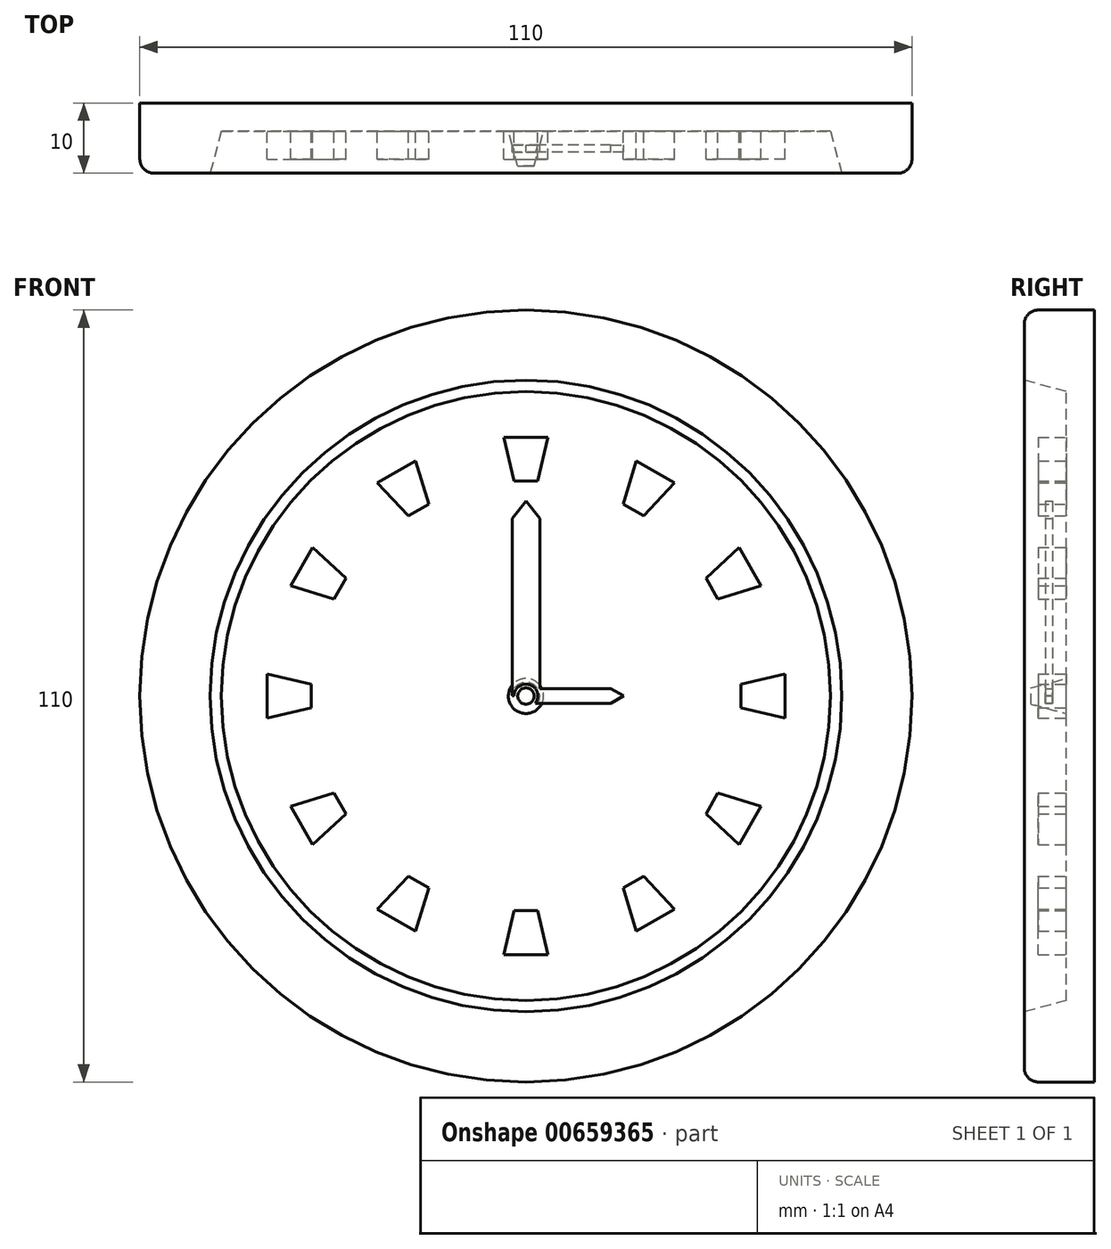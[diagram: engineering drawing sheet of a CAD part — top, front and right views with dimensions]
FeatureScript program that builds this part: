
annotation { "Feature Type Name" : "Feature", "Feature Type Description" : "" }
export const myFeature = defineFeature(function(context is Context, id is Id, definition is map)
    precondition{}
    {
        {
            var Q0;
            Q0=qCreatedBy(makeId("Front.planeOp"),FACE);
            var sketch = newSketch(context, id + "F0", { "sketchPlane" : qUnion([Q0])});
            skCircle(sketch, "E0", {"center": v(0, 0) * mm, "radius": 55 * mm});
            skSolve(sketch);
        }
        {
            var Q0;
            Q0 = qSketchRegion(id + "F0", true);
            extrude(context, id + "F1", {"entities" : qUnion([Q0]), "depth" : 10 * mm, "offsetDistance" : 25 * mm});
        }
        {
            var Q0;
            Q0=makeQuery(id+"F1.opExtrude","CAP_FACE",FACE,{"disambiguationData":[OSD([sQuery(id+"F0.wireOp",EDGE,"E0")])],"isStart":false});
            var sketch = newSketch(context, id + "F2", { "sketchPlane" : qUnion([Q0])});
            skCircle(sketch, "E1", {"center": v(0, 0) * mm, "radius": 45 * mm});
            skSolve(sketch);
        }
        {
            var Q0;
            Q0 = qSketchRegion(id + "F2", true);
            extrude(context, id + "F3", {"entities" : qUnion([Q0]), "operationType" : NewBodyOperationType.REMOVE, "oppositeDirection" : true, "depth" : 6 * mm, "offsetDistance" : 25 * mm, "hasDraft" : true, "draftAngle" : 15 * degree, "draftPullDirection" : true});
        }
        {
            var Q0;
            Q0=makeQuery(id+"F3.boolean.opBoolean","COPY",FACE,{"derivedFrom":makeQuery(id+"F3.opExtrude","CAP_FACE",FACE,{"disambiguationData":[OSD([sQuery(id+"F2.wireOp",EDGE,"E1")])],"isStart":false})});
            var sketch = newSketch(context, id + "F4", { "sketchPlane" : qUnion([Q0])});
            skLineSegment(sketch, "E2", {"start": v(-3.13, 36.9) * mm, "end": v(0, 36.9) * mm});
            skLineSegment(sketch, "E3", {"start": v(0, 36.9) * mm, "end": v(3.13, 36.9) * mm});
            skLineSegment(sketch, "E4", {"start": v(-1.7, 30.6) * mm, "end": v(0, 30.6) * mm});
            skLineSegment(sketch, "E5", {"start": v(0, 30.6) * mm, "end": v(1.7, 30.6) * mm});
            skLineSegment(sketch, "E6", {"start": v(-3.13, 36.9) * mm, "end": v(-1.7, 30.6) * mm});
            skLineSegment(sketch, "E7", {"start": v(3.13, 36.9) * mm, "end": v(1.7, 30.6) * mm});
            skLineSegment(sketch, "E8.1.0", {"start": v(15.73, 33.52) * mm, "end": v(18.45, 31.95) * mm});
            skLineSegment(sketch, "E8.1.1", {"start": v(18.45, 31.95) * mm, "end": v(21.16, 30.38) * mm});
            skLineSegment(sketch, "E8.1.2", {"start": v(15.73, 33.52) * mm, "end": v(13.84, 27.35) * mm});
            skLineSegment(sketch, "E8.1.3", {"start": v(13.84, 27.35) * mm, "end": v(15.3, 26.5) * mm});
            skLineSegment(sketch, "E8.1.4", {"start": v(15.3, 26.5) * mm, "end": v(16.77, 25.66) * mm});
            skLineSegment(sketch, "E8.1.5", {"start": v(21.16, 30.38) * mm, "end": v(16.77, 25.66) * mm});
            skLineSegment(sketch, "E8.2.0", {"start": v(30.38, 21.16) * mm, "end": v(31.95, 18.45) * mm});
            skLineSegment(sketch, "E8.2.1", {"start": v(31.95, 18.45) * mm, "end": v(33.52, 15.73) * mm});
            skLineSegment(sketch, "E8.2.2", {"start": v(30.38, 21.16) * mm, "end": v(25.66, 16.77) * mm});
            skLineSegment(sketch, "E8.2.3", {"start": v(25.66, 16.77) * mm, "end": v(26.5, 15.3) * mm});
            skLineSegment(sketch, "E8.2.4", {"start": v(26.5, 15.3) * mm, "end": v(27.35, 13.84) * mm});
            skLineSegment(sketch, "E8.2.5", {"start": v(33.52, 15.73) * mm, "end": v(27.35, 13.84) * mm});
            skLineSegment(sketch, "E8.3.0", {"start": v(36.9, 3.13) * mm, "end": v(36.9, 0) * mm});
            skLineSegment(sketch, "E8.3.1", {"start": v(36.9, 0) * mm, "end": v(36.9, -3.13) * mm});
            skLineSegment(sketch, "E8.3.2", {"start": v(36.9, 3.13) * mm, "end": v(30.6, 1.7) * mm});
            skLineSegment(sketch, "E8.3.3", {"start": v(30.6, 1.7) * mm, "end": v(30.6, 0) * mm});
            skLineSegment(sketch, "E8.3.4", {"start": v(30.6, 0) * mm, "end": v(30.6, -1.7) * mm});
            skLineSegment(sketch, "E8.3.5", {"start": v(36.9, -3.13) * mm, "end": v(30.6, -1.7) * mm});
            skLineSegment(sketch, "E8.4.0", {"start": v(33.52, -15.73) * mm, "end": v(31.95, -18.45) * mm});
            skLineSegment(sketch, "E8.4.1", {"start": v(31.95, -18.45) * mm, "end": v(30.38, -21.16) * mm});
            skLineSegment(sketch, "E8.4.2", {"start": v(33.52, -15.73) * mm, "end": v(27.35, -13.84) * mm});
            skLineSegment(sketch, "E8.4.3", {"start": v(27.35, -13.84) * mm, "end": v(26.5, -15.3) * mm});
            skLineSegment(sketch, "E8.4.4", {"start": v(26.5, -15.3) * mm, "end": v(25.66, -16.77) * mm});
            skLineSegment(sketch, "E8.4.5", {"start": v(30.38, -21.16) * mm, "end": v(25.66, -16.77) * mm});
            skLineSegment(sketch, "E8.5.0", {"start": v(21.16, -30.38) * mm, "end": v(18.45, -31.95) * mm});
            skLineSegment(sketch, "E8.5.1", {"start": v(18.45, -31.95) * mm, "end": v(15.73, -33.52) * mm});
            skLineSegment(sketch, "E8.5.2", {"start": v(21.16, -30.38) * mm, "end": v(16.77, -25.66) * mm});
            skLineSegment(sketch, "E8.5.3", {"start": v(16.77, -25.66) * mm, "end": v(15.3, -26.5) * mm});
            skLineSegment(sketch, "E8.5.4", {"start": v(15.3, -26.5) * mm, "end": v(13.84, -27.35) * mm});
            skLineSegment(sketch, "E8.5.5", {"start": v(15.73, -33.52) * mm, "end": v(13.84, -27.35) * mm});
            skLineSegment(sketch, "E8.6.0", {"start": v(3.13, -36.9) * mm, "end": v(0, -36.9) * mm});
            skLineSegment(sketch, "E8.6.1", {"start": v(0, -36.9) * mm, "end": v(-3.13, -36.9) * mm});
            skLineSegment(sketch, "E8.6.2", {"start": v(3.13, -36.9) * mm, "end": v(1.7, -30.6) * mm});
            skLineSegment(sketch, "E8.6.3", {"start": v(1.7, -30.6) * mm, "end": v(0, -30.6) * mm});
            skLineSegment(sketch, "E8.6.4", {"start": v(0, -30.6) * mm, "end": v(-1.7, -30.6) * mm});
            skLineSegment(sketch, "E8.6.5", {"start": v(-3.13, -36.9) * mm, "end": v(-1.7, -30.6) * mm});
            skLineSegment(sketch, "E8.7.0", {"start": v(-15.73, -33.52) * mm, "end": v(-18.45, -31.95) * mm});
            skLineSegment(sketch, "E8.7.1", {"start": v(-18.45, -31.95) * mm, "end": v(-21.16, -30.38) * mm});
            skLineSegment(sketch, "E8.7.2", {"start": v(-15.73, -33.52) * mm, "end": v(-13.84, -27.35) * mm});
            skLineSegment(sketch, "E8.7.3", {"start": v(-13.84, -27.35) * mm, "end": v(-15.3, -26.5) * mm});
            skLineSegment(sketch, "E8.7.4", {"start": v(-15.3, -26.5) * mm, "end": v(-16.77, -25.66) * mm});
            skLineSegment(sketch, "E8.7.5", {"start": v(-21.16, -30.38) * mm, "end": v(-16.77, -25.66) * mm});
            skLineSegment(sketch, "E8.8.0", {"start": v(-30.38, -21.16) * mm, "end": v(-31.95, -18.45) * mm});
            skLineSegment(sketch, "E8.8.1", {"start": v(-31.95, -18.45) * mm, "end": v(-33.52, -15.73) * mm});
            skLineSegment(sketch, "E8.8.2", {"start": v(-30.38, -21.16) * mm, "end": v(-25.66, -16.77) * mm});
            skLineSegment(sketch, "E8.8.3", {"start": v(-25.66, -16.77) * mm, "end": v(-26.5, -15.3) * mm});
            skLineSegment(sketch, "E8.8.4", {"start": v(-26.5, -15.3) * mm, "end": v(-27.35, -13.84) * mm});
            skLineSegment(sketch, "E8.8.5", {"start": v(-33.52, -15.73) * mm, "end": v(-27.35, -13.84) * mm});
            skLineSegment(sketch, "E8.9.0", {"start": v(-36.9, -3.13) * mm, "end": v(-36.9, 0) * mm});
            skLineSegment(sketch, "E8.9.1", {"start": v(-36.9, 0) * mm, "end": v(-36.9, 3.13) * mm});
            skLineSegment(sketch, "E8.9.2", {"start": v(-36.9, -3.13) * mm, "end": v(-30.6, -1.7) * mm});
            skLineSegment(sketch, "E8.9.3", {"start": v(-30.6, -1.7) * mm, "end": v(-30.6, 0) * mm});
            skLineSegment(sketch, "E8.9.4", {"start": v(-30.6, 0) * mm, "end": v(-30.6, 1.7) * mm});
            skLineSegment(sketch, "E8.9.5", {"start": v(-36.9, 3.13) * mm, "end": v(-30.6, 1.7) * mm});
            skLineSegment(sketch, "E8.10.0", {"start": v(-33.52, 15.73) * mm, "end": v(-31.95, 18.45) * mm});
            skLineSegment(sketch, "E8.10.1", {"start": v(-31.95, 18.45) * mm, "end": v(-30.38, 21.16) * mm});
            skLineSegment(sketch, "E8.10.2", {"start": v(-33.52, 15.73) * mm, "end": v(-27.35, 13.84) * mm});
            skLineSegment(sketch, "E8.10.3", {"start": v(-27.35, 13.84) * mm, "end": v(-26.5, 15.3) * mm});
            skLineSegment(sketch, "E8.10.4", {"start": v(-26.5, 15.3) * mm, "end": v(-25.66, 16.77) * mm});
            skLineSegment(sketch, "E8.10.5", {"start": v(-30.38, 21.16) * mm, "end": v(-25.66, 16.77) * mm});
            skLineSegment(sketch, "E8.11.0", {"start": v(-21.16, 30.38) * mm, "end": v(-18.45, 31.95) * mm});
            skLineSegment(sketch, "E8.11.1", {"start": v(-18.45, 31.95) * mm, "end": v(-15.73, 33.52) * mm});
            skLineSegment(sketch, "E8.11.2", {"start": v(-21.16, 30.38) * mm, "end": v(-16.77, 25.66) * mm});
            skLineSegment(sketch, "E8.11.3", {"start": v(-16.77, 25.66) * mm, "end": v(-15.3, 26.5) * mm});
            skLineSegment(sketch, "E8.11.4", {"start": v(-15.3, 26.5) * mm, "end": v(-13.84, 27.35) * mm});
            skLineSegment(sketch, "E8.11.5", {"start": v(-15.73, 33.52) * mm, "end": v(-13.84, 27.35) * mm});
            skPoint(sketch, "E8.center", {"position": v(0, 0) * mm});
            skLineSegment(sketch, "E8.anchor1", {"start": v(0, 0) * mm, "end": v(-3.13, 36.9) * mm, "construction": true});
            skLineSegment(sketch, "E8.anchor2", {"start": v(0, 0) * mm, "end": v(-21.16, 30.38) * mm, "construction": true});
            skSolve(sketch);
        }
        {
            var Q0;
            Q0 = qSketchRegion(id + "F4", true);
            extrude(context, id + "F5", {"entities" : qUnion([Q0]), "operationType" : NewBodyOperationType.ADD, "depth" : 4 * mm, "offsetDistance" : 25 * mm});
        }
        {
            var Q0;
            Q0=makeQuery(id+"F1.opExtrude","CAP_FACE",FACE,{"disambiguationData":[OSD([sQuery(id+"F0.wireOp",EDGE,"E0")])],"isStart":false});
            cPlane(context, id + "F6", {"entities" : qUnion([Q0]), "cplaneType" : CPlaneType.OFFSET, "offset" : 0 * mm, "width" : 150 * mm, "height" : 150 * mm});
        }
        {
            var Q0;
            Q0=qCreatedBy(id+"F6.planeOp",FACE);
            var sketch = newSketch(context, id + "F7", { "sketchPlane" : qUnion([Q0])});
            skText(sketch, "E9", { "text": "10", "fontName": "OpenSans-Regular.ttf"});
            skText(sketch, "E10", { "text": "12", "fontName": "OpenSans-Regular.ttf"});
            skText(sketch, "E11", { "text": "9\n", "fontName": "OpenSans-Regular.ttf"});
            skText(sketch, "E12", { "text": "8\n", "fontName": "OpenSans-Regular.ttf"});
            skText(sketch, "E13", { "text": "7\n", "fontName": "OpenSans-Regular.ttf"});
            skText(sketch, "E14", { "text": "6\n", "fontName": "OpenSans-Regular.ttf"});
            skText(sketch, "E15", { "text": "5\n", "fontName": "OpenSans-Regular.ttf"});
            skText(sketch, "E16", { "text": "4\n", "fontName": "OpenSans-Regular.ttf"});
            skText(sketch, "E17", { "text": "3\n", "fontName": "OpenSans-Regular.ttf"});
            skText(sketch, "E18", { "text": "2", "fontName": "OpenSans-Regular.ttf"});
            skText(sketch, "E19", { "text": "1", "fontName": "OpenSans-Regular.ttf"});
            skText(sketch, "E20", { "text": "11", "fontName": "OpenSans-Regular.ttf"});
            const initialGuessF7  = {"E9": [-0.0461, 0.02275, 1, 0, 0.0034], "E10": [-0.0037, 0.04596, 1, 0, 0.00482], "E11": [-0.0523, -0.00214, 1, 0, 0.00596], "E12": [-0.0469, -0.02646, 1, 0, 0.00663], "E13": [-0.0257, -0.04862, 1, 0, 0.0078], "E14": [-0.00248, -0.05388, 1, 0, 0.00769], "E15": [0.0205, -0.04776, 1, 0, 0.00596], "E16": [0.0387, -0.0314, 1, 0, 0.00588], "E17": [0.04789, -0.0041, 1, 0, 0.00675], "E18": [0.04279, 0.01713, 1, 0, 0.00718], "E19": [0.02372, 0.03984, 1, 0, 0.00612], "E20": [-0.02943, 0.04009, 1, 0, 0.0061]};
            skSetInitialGuess(sketch, initialGuessF7);
            skSolve(sketch);
        }
        {
            var Q0;
            Q0 = qSketchRegion(id + "F7", true);
            var Q1;
            Q1 = qConstructionFilter(qBodyType(qCreatedBy(id + "F7" ,EDGE), BodyType.WIRE), ConstructionObject.NO);
            extrude(context, id + "F8", {"entities" : qUnion([Q0]), "bodyType" : ToolBodyType.SURFACE, "surfaceEntities" : qUnion([Q1]), "depth" : 3 * mm, "offsetDistance" : 25 * mm});
        }
        {
            var Q0;
            Q0=makeQuery(id+"F3.boolean.opBoolean","COPY",FACE,{"derivedFrom":makeQuery(id+"F3.opExtrude","CAP_FACE",FACE,{"disambiguationData":[OSD([sQuery(id+"F2.wireOp",EDGE,"E1")])],"isStart":false})});
            cPlane(context, id + "F9", {"entities" : qUnion([Q0]), "cplaneType" : CPlaneType.OFFSET, "offset" : 0 * mm, "width" : 150 * mm, "height" : 150 * mm});
        }
        {
            var Q0;
            Q0=qCreatedBy(id+"F9.planeOp",FACE);
            var sketch = newSketch(context, id + "F10", { "sketchPlane" : qUnion([Q0])});
            skCircle(sketch, "E21", {"center": v(0, 0) * mm, "radius": 2.5 * mm});
            skPoint(sketch, "E22.orphan", {"position": v(0, 2.5) * mm});
            skLineSegment(sketch, "E23", {"start": v(0, 18.56) * mm, "end": v(0, -22.14) * mm});
            skSolve(sketch);
        }
        {
            var Q0;
            Q0 = qSketchRegion(id + "F10", true);
            extrude(context, id + "F11", {"entities" : qUnion([Q0]), "depth" : 5 * mm, "offsetDistance" : 25 * mm, "hasDraft" : true, "draftAngle" : 15 * degree, "draftPullDirection" : true});
        }
        {
            var Q0;
            Q0=makeQuery(id+"F3.boolean.opBoolean","COPY",FACE,{"derivedFrom":makeQuery(id+"F3.opExtrude","CAP_FACE",FACE,{"disambiguationData":[OSD([sQuery(id+"F2.wireOp",EDGE,"E1")])],"isStart":false})});
            cPlane(context, id + "F12", {"entities" : qUnion([Q0]), "cplaneType" : CPlaneType.OFFSET, "offset" : 2 * mm, "width" : 150 * mm, "height" : 150 * mm});
        }
        {
            var Q0;
            Q0=qCreatedBy(id+"F12.planeOp",FACE);
            var sketch = newSketch(context, id + "F13", { "sketchPlane" : qUnion([Q0])});
            skLineSegment(sketch, "E24.bottom", {"start": v(-1.96, 25.29) * mm, "end": v(0, 25.29) * mm});
            skLineSegment(sketch, "E24.top", {"start": v(-1.96, 0) * mm, "end": v(1.96, 0) * mm});
            skLineSegment(sketch, "E24.left", {"start": v(-1.96, 25.29) * mm, "end": v(-1.96, 0) * mm});
            skLineSegment(sketch, "E24.right", {"start": v(1.96, 25.29) * mm, "end": v(1.96, 0) * mm});
            skLineSegment(sketch, "E25", {"start": v(0, 25.29) * mm, "end": v(1.96, 25.29) * mm});
            skLineSegment(sketch, "E26", {"start": v(-1.96, 25.29) * mm, "end": v(0, 27.76) * mm});
            skLineSegment(sketch, "E27", {"start": v(0, 27.76) * mm, "end": v(1.96, 25.29) * mm});
            skSolve(sketch);
        }
        {
            var Q0;
            Q0 = qSketchRegion(id + "F13", true);
            extrude(context, id + "F14", {"entities" : qUnion([Q0]), "operationType" : NewBodyOperationType.ADD, "depth" : 1 * mm, "offsetDistance" : 25 * mm});
        }
        {
            var Q0;
            Q0=qCreatedBy(id+"F12.planeOp",FACE);
            var sketch = newSketch(context, id + "F15", { "sketchPlane" : qUnion([Q0])});
            skLineSegment(sketch, "E28.bottom", {"start": v(12.1, 1.05) * mm, "end": v(0, 1.05) * mm});
            skLineSegment(sketch, "E28.top", {"start": v(12.1, -1.05) * mm, "end": v(0, -1.05) * mm});
            skLineSegment(sketch, "E28.left", {"start": v(12.1, 1.05) * mm, "end": v(12.1, 0) * mm});
            skLineSegment(sketch, "E28.right", {"start": v(0, 1.05) * mm, "end": v(0, -1.05) * mm});
            skLineSegment(sketch, "E29", {"start": v(12.1, 0) * mm, "end": v(12.1, -1.05) * mm});
            skLineSegment(sketch, "E30", {"start": v(12.1, 1.05) * mm, "end": v(13.91, 0) * mm});
            skLineSegment(sketch, "E31", {"start": v(13.91, 0) * mm, "end": v(12.1, -1.05) * mm});
            skSolve(sketch);
        }
        {
            var Q0;
            Q0 = qSketchRegion(id + "F15", true);
            extrude(context, id + "F16", {"entities" : qUnion([Q0]), "operationType" : NewBodyOperationType.ADD, "depth" : 1 * mm, "offsetDistance" : 25 * mm});
        }
        {
            var Q0;
            Q0=makeQuery(id+"F1.opExtrude","CAP_EDGE",EDGE,{"disambiguationData":[OSD([sQuery(id+"F0.wireOp",EDGE,"E0")])],"isStart":false});
            fillet(context, id + "F17", {"entities" : qUnion([Q0]), "radius" : 2 * mm, "tangentPropagation" : true, "allowEdgeOverflow" : false});
        }
    });
